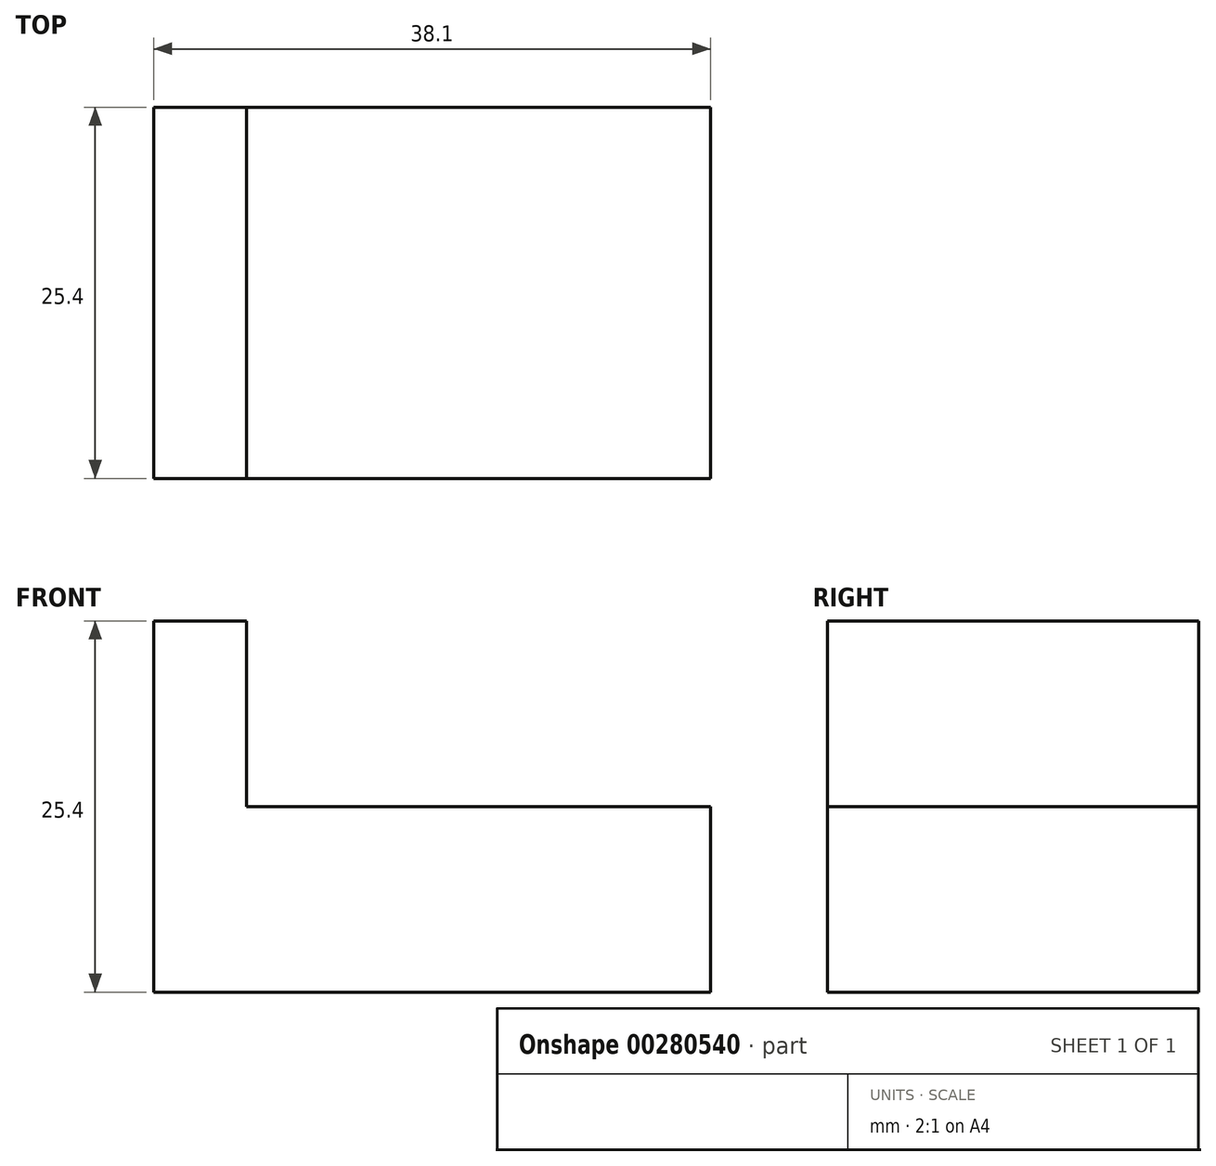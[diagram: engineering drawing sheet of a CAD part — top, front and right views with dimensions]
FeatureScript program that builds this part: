
annotation { "Feature Type Name" : "Feature", "Feature Type Description" : "" }
export const myFeature = defineFeature(function(context is Context, id is Id, definition is map)
    precondition{}
    {
        {
            var Q0;
            Q0=qCreatedBy(makeId("Front.planeOp"),FACE);
            var sketch = newSketch(context, id + "F0", { "sketchPlane" : qUnion([Q0])});
            skLineSegment(sketch, "E0", {"start": v(0, 0) * mm, "end": v(0, 25.4) * mm});
            skLineSegment(sketch, "E1", {"start": v(0, 25.4) * mm, "end": v(6.35, 25.4) * mm});
            skLineSegment(sketch, "E2", {"start": v(0, 0) * mm, "end": v(38.1, 0) * mm});
            skLineSegment(sketch, "E3", {"start": v(38.1, 0) * mm, "end": v(38.1, 12.7) * mm});
            skLineSegment(sketch, "E4", {"start": v(38.1, 12.7) * mm, "end": v(6.35, 12.7) * mm});
            skLineSegment(sketch, "E5", {"start": v(6.35, 25.4) * mm, "end": v(6.35, 12.7) * mm});
            skSolve(sketch);
        }
        {
            var Q0;
            Q0=makeQuery(id+"F0.imprint","IMPRINT",FACE,{"disambiguationData":[TD([[makeQuery(id+"F0.imprint","IMPRINT",EDGE,{"derivedFrom":sQuery(id+"F0.wireOp",EDGE,"E0")}),-1.0]])]});
            extrude(context, id + "F1", {"entities" : qUnion([Q0]), "oppositeDirection" : true, "depth" : 25.4 * mm});
        }
    });
